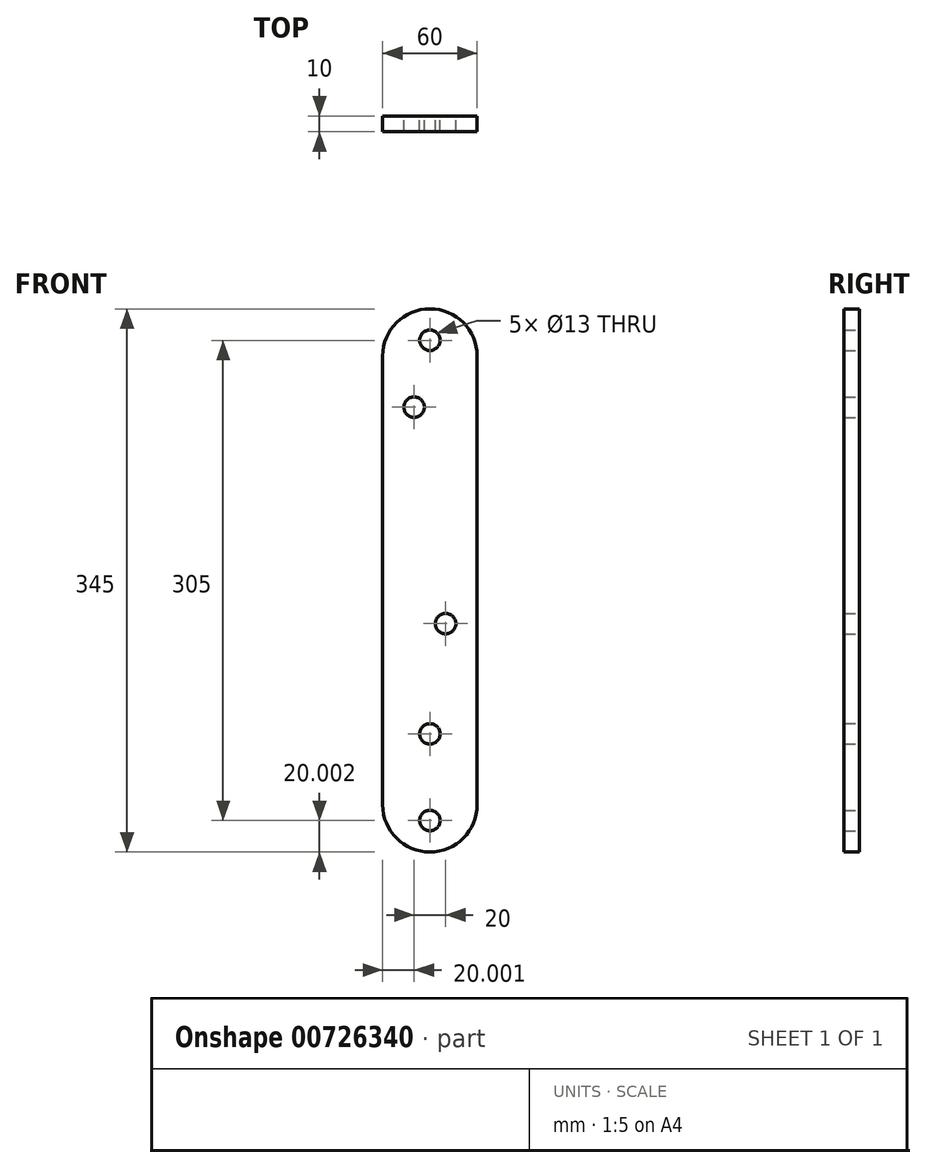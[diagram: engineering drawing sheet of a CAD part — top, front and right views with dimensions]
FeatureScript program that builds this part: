
annotation { "Feature Type Name" : "Feature", "Feature Type Description" : "" }
export const myFeature = defineFeature(function(context is Context, id is Id, definition is map)
    precondition{}
    {
        {
            var Q0;
            Q0=qCreatedBy(makeId("Front.planeOp"),FACE);
            var sketch = newSketch(context, id + "F0", { "sketchPlane" : qUnion([Q0])});
            skLineSegment(sketch, "E0", {"start": v(-45.12, 269.95) * mm, "end": v(-45.12, -15.05) * mm});
            skLineSegment(sketch, "E1", {"start": v(14.88, 269.95) * mm, "end": v(14.88, -15.05) * mm});
            skArc(sketch, "E2", {"start": v(14.88, 269.95) * mm, "mid": v(-15.12, 299.95) * mm, "end": v(-45.12, 269.95) * mm});
            skArc(sketch, "E3", {"start": v(-45.12, -15.05) * mm, "mid": v(-15.12, -45.05) * mm, "end": v(14.88, -15.05) * mm});
            skLineSegment(sketch, "E4", {"start": v(-15.12, 321.16) * mm, "end": v(-15.12, -130.72) * mm, "construction": true});
            skLineSegment(sketch, "E5", {"start": v(-76.86, 99.95) * mm, "end": v(58.35, 99.95) * mm, "construction": true});
            skPoint(sketch, "E6", {"position": v(-15.12, -25.05) * mm});
            skPoint(sketch, "E7", {"position": v(-15.12, 29.95) * mm});
            skPoint(sketch, "E8", {"position": v(-15.12, 279.95) * mm});
            skLineSegment(sketch, "E9", {"start": v(-5.12, 312.88) * mm, "end": v(-5.12, -101.4) * mm, "construction": true});
            skPoint(sketch, "E10", {"position": v(-5.12, 99.95) * mm});
            skLineSegment(sketch, "E11", {"start": v(-25.12, 310.87) * mm, "end": v(-25.12, -84.1) * mm, "construction": true});
            skPoint(sketch, "E12", {"position": v(-25.12, 237.45) * mm});
            skSolve(sketch);
        }
        {
            var Q0;
            Q0 = qSketchRegion(id + "F0", true);
            extrude(context, id + "F1", {"entities" : qUnion([Q0]), "depth" : 10 * mm, "offsetDistance" : 25 * mm});
        }
        {
            var Q0;
            Q0=sQuery(id+"F0.wireOp",VERTEX,"E7");
            var Q1;
            Q1=sQuery(id+"F0.wireOp",VERTEX,"E6");
            var Q2;
            Q2=makeQuery(id+"F1.opExtrude","SWEPT_BODY",BODY,{"disambiguationData":[OSD([sQuery(id+"F0.wireOp",EDGE,"E0"),sQuery(id+"F0.wireOp",EDGE,"E1"),sQuery(id+"F0.wireOp",EDGE,"E2"),sQuery(id+"F0.wireOp",EDGE,"E3")])]});
            hole(context, id + "F2", {"style" : HoleStyle.SIMPLE, "endStyle" : HoleEndStyle.THROUGH, "oppositeDirection" : true, "holeDiameter" : 13 * mm, "majorDiameter" : 5 * mm, "isTappedThrough" : true, "tappedDepth" : 12 * mm, "tapClearance" : 3, "locations" : qUnion([Q0, Q1]), "scope" : qUnion([Q2])});
        }
        {
            var Q0;
            Q0=sQuery(id+"F0.wireOp",VERTEX,"E8");
            var Q1;
            Q1=makeQuery(id+"F1.opExtrude","SWEPT_BODY",BODY,{"disambiguationData":[OSD([sQuery(id+"F0.wireOp",EDGE,"E0"),sQuery(id+"F0.wireOp",EDGE,"E1"),sQuery(id+"F0.wireOp",EDGE,"E2"),sQuery(id+"F0.wireOp",EDGE,"E3")])]});
            hole(context, id + "F3", {"style" : HoleStyle.SIMPLE, "endStyle" : HoleEndStyle.THROUGH, "oppositeDirection" : true, "holeDiameter" : 13 * mm, "majorDiameter" : 5 * mm, "isTappedThrough" : true, "tappedDepth" : 12 * mm, "tapClearance" : 3, "locations" : qUnion([Q0]), "scope" : qUnion([Q1])});
        }
        {
            var Q0;
            Q0=sQuery(id+"F0.wireOp",VERTEX,"E12");
            var Q1;
            Q1=sQuery(id+"F0.wireOp",VERTEX,"E10");
            var Q2;
            Q2=makeQuery(id+"F1.opExtrude","SWEPT_BODY",BODY,{"disambiguationData":[OSD([sQuery(id+"F0.wireOp",EDGE,"E0"),sQuery(id+"F0.wireOp",EDGE,"E1"),sQuery(id+"F0.wireOp",EDGE,"E2"),sQuery(id+"F0.wireOp",EDGE,"E3")])]});
            hole(context, id + "F4", {"style" : HoleStyle.SIMPLE, "endStyle" : HoleEndStyle.THROUGH, "oppositeDirection" : true, "holeDiameter" : 13 * mm, "majorDiameter" : 5 * mm, "isTappedThrough" : true, "tappedDepth" : 12 * mm, "tapClearance" : 3, "locations" : qUnion([Q0, Q1]), "scope" : qUnion([Q2])});
        }
    });
